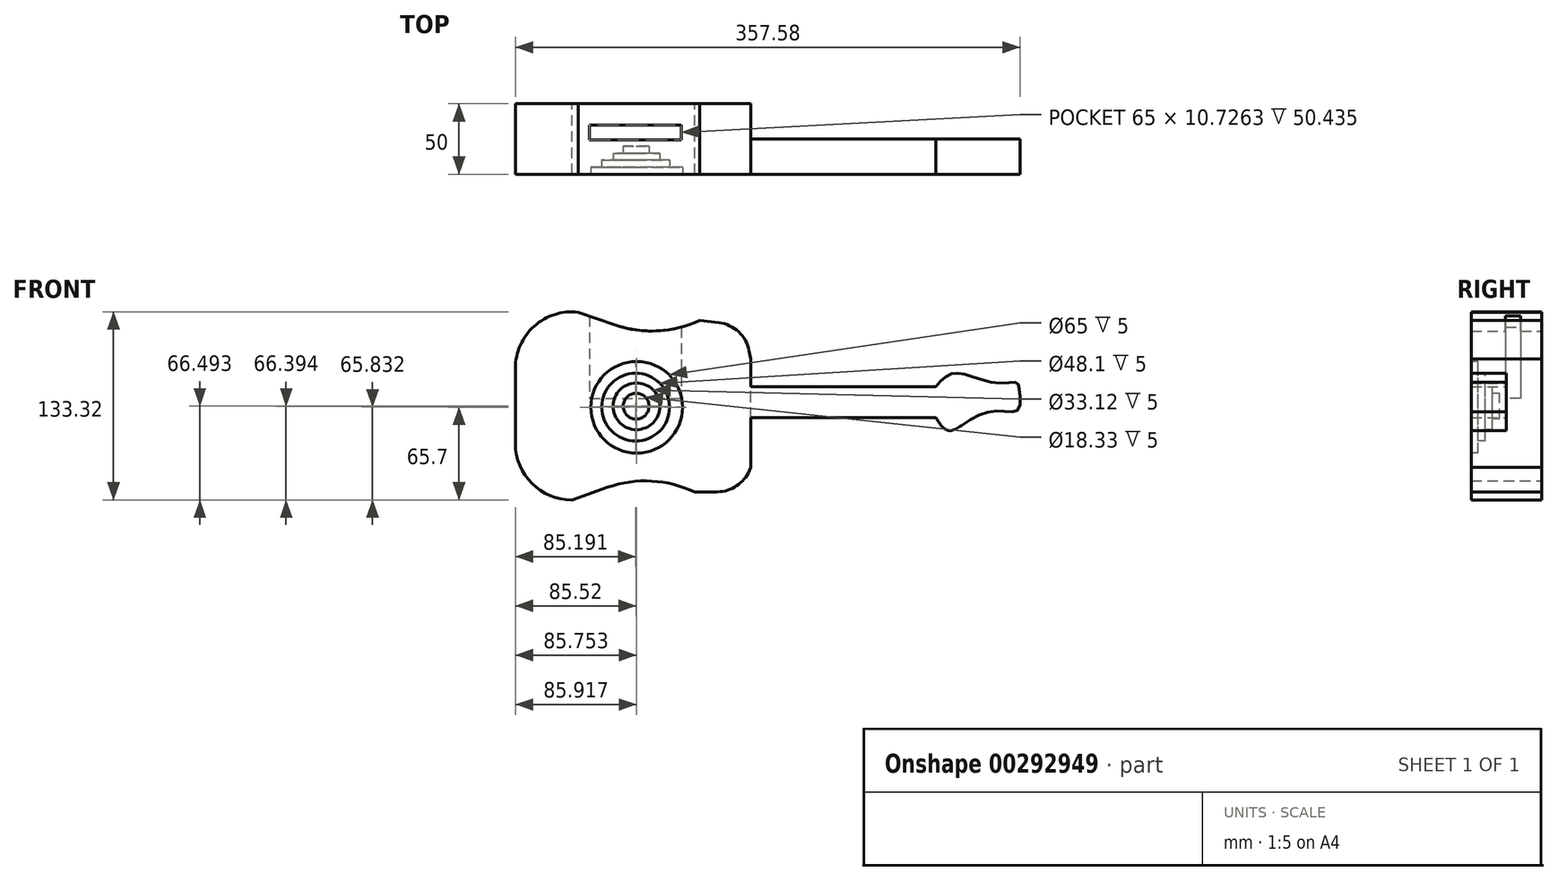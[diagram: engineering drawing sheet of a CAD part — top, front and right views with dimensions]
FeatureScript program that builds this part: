
annotation { "Feature Type Name" : "Feature", "Feature Type Description" : "" }
export const myFeature = defineFeature(function(context is Context, id is Id, definition is map)
    precondition{}
    {
        {
            var Q0;
            Q0=qCreatedBy(makeId("Front.planeOp"),FACE);
            var sketch = newSketch(context, id + "F0", { "sketchPlane" : qUnion([Q0])});
            skLineSegment(sketch, "E0.top", {"start": v(-111.35, -72.05) * mm, "end": v(-110.9, -72.05) * mm});
            skLineSegment(sketch, "E0.left", {"start": v(-178.56, 21.27) * mm, "end": v(-178.56, -32.05) * mm});
            skPoint(sketch, "E1.visualSharp", {"position": v(-178.56, 57.95) * mm});
            skArc(sketch, "E1.filletArc", {"start": v(-134.01, 61) * mm, "mid": v(-165.19, 51.12) * mm, "end": v(-178.56, 21.27) * mm});
            skPoint(sketch, "E2.visualSharp", {"position": v(-178.56, -72.05) * mm});
            skArc(sketch, "E2.filletArc", {"start": v(-178.56, -32.05) * mm, "mid": v(-166.85, -60.33) * mm, "end": v(-138.56, -72.05) * mm});
            skLineSegment(sketch, "E3", {"start": v(-110.9, 57.95) * mm, "end": v(-110.9, 57.95) * mm});
            skLineSegment(sketch, "E4", {"start": v(-110.9, -72.05) * mm, "end": v(-110.9, -72.05) * mm});
            skPoint(sketch, "E5.visualSharp", {"position": v(-110.9, 57.95) * mm});
            skPoint(sketch, "E6.visualSharp", {"position": v(-110.9, -72.05) * mm});
            skLineSegment(sketch, "E7.filletArc", {"start": v(-111.19, 57.95) * mm, "end": v(-111.19, 57.95) * mm});
            skPoint(sketch, "E8.newPointA", {"position": v(171.44, 58.9) * mm});
            skLineSegment(sketch, "E8.filletArc", {"start": v(-35.65, 61) * mm, "end": v(-35.65, 61) * mm});
            skLineSegment(sketch, "E9", {"start": v(-134.01, 61) * mm, "end": v(-107.97, 52.03) * mm});
            skPoint(sketch, "E10.visualSharp", {"position": v(-77.29, 41.46) * mm});
            skArc(sketch, "E10.filletArc", {"start": v(-107.97, 52.03) * mm, "mid": v(-77.62, 47.78) * mm, "end": v(-47.9, 55.25) * mm});
            skPoint(sketch, "E11.orphan", {"position": v(-178.56, -93.5) * mm});
            skLineSegment(sketch, "E12", {"start": v(-138.56, -72.05) * mm, "end": v(-113.05, -63.06) * mm});
            skPoint(sketch, "E13.end.orphan", {"position": v(-77.34, 61) * mm});
            skPoint(sketch, "E14.visualSharp", {"position": v(-81.59, -51.98) * mm});
            skArc(sketch, "E14.filletArc", {"start": v(-51.57, -66.53) * mm, "mid": v(-81.96, -58.65) * mm, "end": v(-113.05, -63.06) * mm});
            skLineSegment(sketch, "E15", {"start": v(-35.65, 61) * mm, "end": v(-31.87, 61) * mm});
            skPoint(sketch, "E16.visualSharp", {"position": v(-3.25, 61) * mm});
            skPoint(sketch, "E17.visualSharp", {"position": v(-18.28, -75.81) * mm});
            skLineSegment(sketch, "E18", {"start": v(-11.87, -49) * mm, "end": v(-12.74, -51.06) * mm});
            skPoint(sketch, "E18.endSnap0", {"position": v(-19, -66.15) * mm});
            skLineSegment(sketch, "E19", {"start": v(-35.49, -66.34) * mm, "end": v(-51.57, -66.53) * mm});
            skPoint(sketch, "E20.visualSharp", {"position": v(-19.1, 52.23) * mm});
            skPoint(sketch, "E21.visualSharp", {"position": v(-19.1, -66.15) * mm});
            skArc(sketch, "E21.filletArc", {"start": v(-35.49, -66.34) * mm, "mid": v(-21.83, -62.1) * mm, "end": v(-12.74, -51.06) * mm});
            skLineSegment(sketch, "E22", {"start": v(-11.87, 28.04) * mm, "end": v(-12.96, 33.61) * mm});
            skLineSegment(sketch, "E23", {"start": v(-34.5, 53.64) * mm, "end": v(-47.9, 55.25) * mm});
            skPoint(sketch, "E24.end.orphan", {"position": v(-9.68, 33.85) * mm});
            skPoint(sketch, "E25.visualSharp", {"position": v(-16.45, 51.47) * mm});
            skArc(sketch, "E25.filletArc", {"start": v(-12.96, 33.61) * mm, "mid": v(-20.48, 47.13) * mm, "end": v(-34.5, 53.64) * mm});
            skLineSegment(sketch, "E26", {"start": v(-110.9, -72.05) * mm, "end": v(-111.35, -72.05) * mm});
            skPoint(sketch, "E27.start.orphan", {"position": v(-9.68, -13.76) * mm});
            skLineSegment(sketch, "E28", {"start": v(-11.87, -49) * mm, "end": v(-11.87, -13.76) * mm});
            skPoint(sketch, "E29.orphan", {"position": v(-12.1, -72.05) * mm});
            skLineSegment(sketch, "E30", {"start": v(119.2, 8.15) * mm, "end": v(-11.87, 8.15) * mm});
            skLineSegment(sketch, "E31", {"start": v(-11.87, -13.76) * mm, "end": v(119.2, -13.76) * mm});
            skLineSegment(sketch, "E32", {"start": v(138.33, -18.76) * mm, "end": v(138.48, -18.76) * mm});
            skPoint(sketch, "E33.end.orphan", {"position": v(138.33, 8.15) * mm});
            skPoint(sketch, "E34.start.orphan", {"position": v(138.33, -13.76) * mm});
            skLineSegment(sketch, "E35.trimOffspring", {"start": v(-11.87, 8.15) * mm, "end": v(-11.87, 28.04) * mm});
            skFitSpline(sketch, "E36", {"points": [v(119.2, -13.76) * mm, v(128.77, -22.89) * mm, v(146.2, -13.76) * mm, v(165.69, -9) * mm, v(177.56, -8.1) * mm, v(178.46, 6.24) * mm, v(176.9, 10.95) * mm, v(162.55, 10.95) * mm, v(140.6, 16.77) * mm, v(128.77, 16.77) * mm, v(119.2, 8.15) * mm, v(111.69, 0) * mm], "startDerivative": vector(95.93, -149.43) * mm, "endDerivative": vector(-89.6, -94.88) * mm});
            skPoint(sketch, "E37.end.orphan", {"position": v(128.77, 8.15) * mm});
            skPoint(sketch, "E38.end.orphan", {"position": v(128.77, 13.15) * mm});
            skPoint(sketch, "E39.end.orphan", {"position": v(128.77, -18.76) * mm});
            skPoint(sketch, "E39.start.orphan", {"position": v(128.77, -13.76) * mm});
            skSolve(sketch);
        }
        {
            var Q0;
            Q0 = qSketchRegion(id + "F0", true);
            extrude(context, id + "F1", {"entities" : qUnion([Q0]), "depth" : 50 * mm});
        }
        {
            var Q0;
            Q0=makeQuery(id+"F1.opExtrude","SWEPT_FACE",FACE,{"disambiguationData":[OSD([sQuery(id+"F0.wireOp",EDGE,"E30")])]});
            var sketch = newSketch(context, id + "F2", { "sketchPlane" : qUnion([Q0])});
            skLineSegment(sketch, "E40.bottom", {"start": v(-11.87, 0) * mm, "end": v(191.53, 0) * mm});
            skLineSegment(sketch, "E40.top", {"start": v(-11.87, -25) * mm, "end": v(191.53, -25) * mm});
            skLineSegment(sketch, "E40.left", {"start": v(-11.87, 0) * mm, "end": v(-11.87, -25) * mm});
            skLineSegment(sketch, "E40.right", {"start": v(191.53, 0) * mm, "end": v(191.53, -25) * mm});
            skSolve(sketch);
        }
        {
            var Q0;
            Q0 = qSketchRegion(id + "F2", true);
            extrude(context, id + "F3", {"entities" : qUnion([Q0]), "operationType" : NewBodyOperationType.REMOVE, "endBound" : BoundingType.SYMMETRIC, "oppositeDirection" : true, "depth" : 80.8 * mm});
        }
        {
            var Q0;
            Q0=qCreatedBy(makeId("Top.planeOp"),FACE);
            var sketch = newSketch(context, id + "F4", { "sketchPlane" : qUnion([Q0])});
            skLineSegment(sketch, "E41.bottom", {"start": v(-126.05, -15) * mm, "end": v(-61.05, -15) * mm});
            skLineSegment(sketch, "E41.top", {"start": v(-126.05, -25.73) * mm, "end": v(-61.05, -25.73) * mm});
            skLineSegment(sketch, "E41.left", {"start": v(-126.05, -15) * mm, "end": v(-126.05, -25.73) * mm});
            skLineSegment(sketch, "E41.right", {"start": v(-61.05, -15) * mm, "end": v(-61.05, -25.73) * mm});
            skSolve(sketch);
        }
        {
            var Q0;
            Q0 = qSketchRegion(id + "F4", true);
            extrude(context, id + "F5", {"entities" : qUnion([Q0]), "operationType" : NewBodyOperationType.REMOVE, "depth" : 112 * mm});
        }
        {
            var Q0;
            Q0=makeQuery(id+"F1.opExtrude","CAP_FACE",FACE,{"disambiguationData":[OSD([sQuery(id+"F0.wireOp",EDGE,"E0.left"),sQuery(id+"F0.wireOp",EDGE,"E1.filletArc"),sQuery(id+"F0.wireOp",EDGE,"E2.filletArc"),sQuery(id+"F0.wireOp",EDGE,"E9"),sQuery(id+"F0.wireOp",EDGE,"E10.filletArc"),sQuery(id+"F0.wireOp",EDGE,"E12"),sQuery(id+"F0.wireOp",EDGE,"E14.filletArc"),sQuery(id+"F0.wireOp",EDGE,"E18"),sQuery(id+"F0.wireOp",EDGE,"E19"),sQuery(id+"F0.wireOp",EDGE,"E21.filletArc"),sQuery(id+"F0.wireOp",EDGE,"E22"),sQuery(id+"F0.wireOp",EDGE,"E23"),sQuery(id+"F0.wireOp",EDGE,"E25.filletArc"),sQuery(id+"F0.wireOp",EDGE,"E28"),sQuery(id+"F0.wireOp",EDGE,"E30"),sQuery(id+"F0.wireOp",EDGE,"E31"),sQuery(id+"F0.wireOp",EDGE,"E35.trimOffspring"),sQuery(id+"F0.wireOp",EDGE,"E36")])],"isStart":false});
            var sketch = newSketch(context, id + "F6", { "sketchPlane" : qUnion([Q0])});
            skCircle(sketch, "E42", {"center": v(-92.64, -6.35) * mm, "radius": 32.5 * mm});
            skSolve(sketch);
        }
        {
            var Q0;
            Q0=makeQuery(id+"F6.imprint","IMPRINT",FACE,{"disambiguationData":[TD([[makeQuery(id+"F6.imprint","IMPRINT",EDGE,{"derivedFrom":sQuery(id+"F6.wireOp",EDGE,"E42")}),-1.0]])]});
            var sketch = newSketch(context, id + "F7", { "sketchPlane" : qUnion([Q0])});
            skCircle(sketch, "E43", {"center": v(-93.37, -6.22) * mm, "radius": 24.05 * mm});
            skSolve(sketch);
        }
        {
            var Q0;
            Q0=makeQuery(id+"F6.imprint","IMPRINT",FACE,{"disambiguationData":[TD([[makeQuery(id+"F6.imprint","IMPRINT",EDGE,{"derivedFrom":sQuery(id+"F6.wireOp",EDGE,"E42")}),-1.0]])]});
            var sketch = newSketch(context, id + "F8", { "sketchPlane" : qUnion([Q0])});
            skCircle(sketch, "E44", {"center": v(-92.8, -5.66) * mm, "radius": 16.56 * mm});
            skSolve(sketch);
        }
        {
            var Q0;
            Q0=makeQuery(id+"F7.imprint","IMPRINT",FACE,{"disambiguationData":[TD([[makeQuery(id+"F7.imprint","IMPRINT",EDGE,{"derivedFrom":makeQuery(id+"F6.imprint","IMPRINT",EDGE,{"derivedFrom":sQuery(id+"F6.wireOp",EDGE,"E42")})}),-1.0]])]});
            var sketch = newSketch(context, id + "F9", { "sketchPlane" : qUnion([Q0])});
            skCircle(sketch, "E45", {"center": v(-93.04, -5.56) * mm, "radius": 9.16 * mm});
            skSolve(sketch);
        }
        {
            var Q0;
            Q0 = qSketchRegion(id + "F6", true);
            extrude(context, id + "F10", {"entities" : qUnion([Q0]), "operationType" : NewBodyOperationType.REMOVE, "oppositeDirection" : true, "depth" : 5 * mm});
        }
        {
            var Q0;
            Q0 = qSketchRegion(id + "F7", true);
            extrude(context, id + "F11", {"entities" : qUnion([Q0]), "operationType" : NewBodyOperationType.REMOVE, "oppositeDirection" : true, "depth" : 10 * mm});
        }
        {
            var Q0;
            Q0 = qSketchRegion(id + "F8", true);
            extrude(context, id + "F12", {"entities" : qUnion([Q0]), "operationType" : NewBodyOperationType.REMOVE, "oppositeDirection" : true, "depth" : 15 * mm});
        }
        {
            var Q0;
            Q0 = qSketchRegion(id + "F9", true);
            extrude(context, id + "F13", {"entities" : qUnion([Q0]), "operationType" : NewBodyOperationType.REMOVE, "oppositeDirection" : true, "depth" : 20 * mm});
        }
    });
